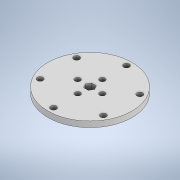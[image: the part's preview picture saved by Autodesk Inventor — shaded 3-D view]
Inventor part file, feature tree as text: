
AUTODESK INVENTOR PART (.ipt)
format: ipt  version: 2020 (Build 240168000, 168)  size: 159,232 bytes
history: native  units: in
note: dims shown in document units (in); Inventor stores cm internally (conversion verified against a paired STEP export)
features: extrude x5, sketch x5, plane x2, pattern_circular x2, other x1
ambient origin geometry x8: Origin, YZ Plane, XZ Plane, XY Plane, X Axis, Y Axis, Z Axis, Center Point
bodies: Solid1 (feature_tree)
feature tree (15):
  extrude  "Extrusion1"  Depth=0.3in TaperAngle=0.0deg
  plane  "Work Plane5"
  extrude  "Extrusion4"  Depth=1.0in TaperAngle=0.0deg
  extrude  "Extrusion5"  Depth=0.075in
  plane  "Work Plane6"
  other  "Work Axis1"
  pattern_circular  "Circular Pattern1"  Count=6 Angle=360.0deg
  extrude  "Extrusion6"  Depth=0.07in
  pattern_circular  "Circular Pattern2"  [2 undecoded]
  extrude  "Extrusion8"  Depth=0.15in TaperAngle=360.0deg
  sketch  "Sketch1"  dims[d0=2.2in d1=0.3in d2=0.0in]
  sketch  "Sketch5"  dims[d10=0.105in d11=1.0in d12=0.0in]
  sketch  "Sketch6"  dims[d13=0.07in d14=0.075in]
  sketch  "Sketch8"  dims[d15=1.0in d16=0.0in d17=2.3622in d18=360.0deg]
  sketch  "Sketch10"  dims[d20=0.13in d21=0.07in d22=1.0in d23=0.0in d24=1.5748in d25=360.0deg d30=0.15in d31=0.0in d27=0.5in d28=0.0344in d29=0.5in]
note: 2 required parameter values undecoded (feature->parameter linkage not recoverable at this tier; creation-order binding heuristic only, values carry confidence <= 0.55)
